# Revit family: 34166_912350SC_BK_File_Rfa_149402_ori_2014Aug15142524
name_source: partatom
category: Plumbing Fixtures
units: mm (PartAtom-declared; Revit-internal decimal feet)

## family parameters
Cut with Voids When Loaded = Yes
Host = Face
OmniClass Number = 23.45.05.21.11.11
OmniClass Title = Water Operated Water Closets
Part Type = Normal
Room Calculation Point = No
Round Connector Dimension = Use Diameter
Shared = No

## types (1)
- Standard
    Assembly Code = D2010110
    CW Connection = Yes
    CWFU = 2
    Default Elevation = 0 mm  [stored 0 ft]
    Description = Caroma Profile II Close Coupled Suite
    HW Connection = No
    Hardware = Metal-Chrome-Caroma
    Height_ANZRS = 792 mm  [stored 2.59843 ft]
    Keynote = WC
    Length_ANZRS = 665 mm  [stored 2.18176 ft]
    Manufacturer = GWA Bathrooms & Kitchens
    Material_ANZRS = Porcelain-White-Caroma
    Model = 912350W
    ModifiedIssue_ANZRS = 20140627.01 $
    Type Comments = Vitreous China, White Only, S or P Trap available, Bottom Inlet Cistern, Mirage Close Coupled Pan, Chrome Button Assembly
    URL = http://www.caroma.com.au
    Vent Connection = No
    WELSRating_ANZRS = WELS 4 Star rated, 4.5/3L
    WFU = 3
    Waste Connection = Yes
    WasteOutlet_ANZRS = 0
    Width_ANZRS = 406 mm  [stored 1.33202 ft]

note: [stored X ft] marks values corroborated as IEEE doubles in the binary element streams (Revit-internal decimal feet)

## geometry (parser evidence)
native form markers: Blend x8, Sweep x1
no freeform markers — native parametric forms only
